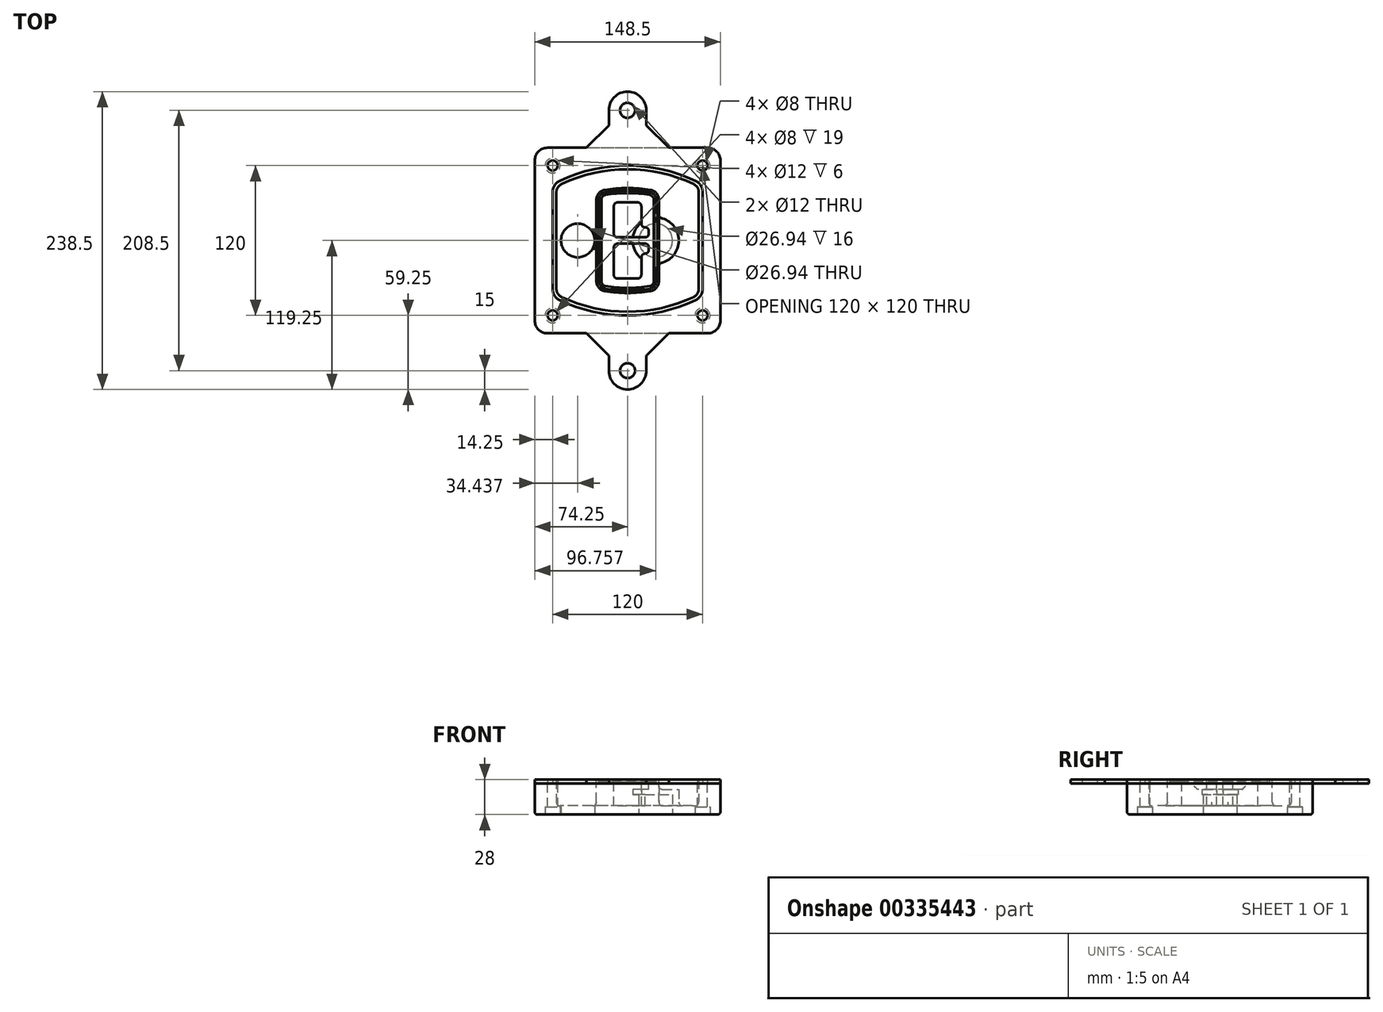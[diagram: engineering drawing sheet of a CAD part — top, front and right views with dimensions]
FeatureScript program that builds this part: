
annotation { "Feature Type Name" : "Feature", "Feature Type Description" : "" }
export const myFeature = defineFeature(function(context is Context, id is Id, definition is map)
    precondition{}
    {
        {
            var Q0;
            Q0=qCreatedBy(makeId("Top.planeOp"),FACE);
            var sketch = newSketch(context, id + "F0", { "sketchPlane" : qUnion([Q0])});
            skPoint(sketch, "E0.rect.middle", {"position": v(0, 0) * mm});
            skLineSegment(sketch, "E1.bottom", {"start": v(-64.25, -74.25) * mm, "end": v(64.25, -74.25) * mm});
            skLineSegment(sketch, "E1.top", {"start": v(-64.25, 74.25) * mm, "end": v(64.25, 74.25) * mm});
            skLineSegment(sketch, "E1.left", {"start": v(-74.25, -64.25) * mm, "end": v(-74.25, 64.25) * mm});
            skLineSegment(sketch, "E1.right", {"start": v(74.25, -64.25) * mm, "end": v(74.25, 64.25) * mm});
            skLineSegment(sketch, "E2", {"start": v(-74.25, 74.25) * mm, "end": v(74.25, -74.25) * mm, "construction": true});
            skLineSegment(sketch, "E3", {"start": v(74.25, 74.25) * mm, "end": v(-74.25, -74.25) * mm, "construction": true});
            skCircle(sketch, "E4", {"center": v(-60, 60) * mm, "radius": 4 * mm});
            skCircle(sketch, "E5", {"center": v(60, 60) * mm, "radius": 4 * mm});
            skCircle(sketch, "E6", {"center": v(60, -60) * mm, "radius": 4 * mm});
            skCircle(sketch, "E7", {"center": v(-60, -60) * mm, "radius": 4 * mm});
            skLineSegment(sketch, "E8", {"start": v(-60, 60) * mm, "end": v(60, 60) * mm, "construction": true});
            skLineSegment(sketch, "E9", {"start": v(60, 60) * mm, "end": v(60, -60) * mm, "construction": true});
            skLineSegment(sketch, "E10", {"start": v(60, -60) * mm, "end": v(-60, -60) * mm, "construction": true});
            skLineSegment(sketch, "E11", {"start": v(-60, -60) * mm, "end": v(-60, 60) * mm, "construction": true});
            skLineSegment(sketch, "E12", {"start": v(-60, 38.83) * mm, "end": v(-60, -38.83) * mm});
            skLineSegment(sketch, "E13", {"start": v(60, 38.83) * mm, "end": v(60, -38.83) * mm});
            skArc(sketch, "E14", {"start": v(54.26, 47.88) * mm, "mid": v(0, 60) * mm, "end": v(-54.26, 47.88) * mm});
            skArc(sketch, "E15", {"start": v(-54.26, -47.88) * mm, "mid": v(0, -60) * mm, "end": v(54.26, -47.88) * mm});
            skLineSegment(sketch, "E16", {"start": v(-60, 0) * mm, "end": v(60, 0) * mm, "construction": true});
            skPoint(sketch, "E17.visualSharp", {"position": v(-60, -45) * mm});
            skArc(sketch, "E17.filletArc", {"start": v(-60, -38.83) * mm, "mid": v(-58.44, -44.2) * mm, "end": v(-54.26, -47.88) * mm});
            skPoint(sketch, "E18.visualSharp", {"position": v(-60, 45) * mm});
            skArc(sketch, "E18.filletArc", {"start": v(-54.26, 47.88) * mm, "mid": v(-58.44, 44.2) * mm, "end": v(-60, 38.83) * mm});
            skPoint(sketch, "E19.visualSharp", {"position": v(60, 45) * mm});
            skArc(sketch, "E19.filletArc", {"start": v(60, 38.83) * mm, "mid": v(58.44, 44.2) * mm, "end": v(54.26, 47.88) * mm});
            skPoint(sketch, "E20.visualSharp", {"position": v(60, -45) * mm});
            skArc(sketch, "E20.filletArc", {"start": v(54.26, -47.88) * mm, "mid": v(58.44, -44.2) * mm, "end": v(60, -38.83) * mm});
            skPoint(sketch, "E21.visualSharp", {"position": v(-74.25, 74.25) * mm});
            skArc(sketch, "E21.filletArc", {"start": v(-64.25, 74.25) * mm, "mid": v(-71.32, 71.32) * mm, "end": v(-74.25, 64.25) * mm});
            skPoint(sketch, "E22.visualSharp", {"position": v(74.25, 74.25) * mm});
            skArc(sketch, "E22.filletArc", {"start": v(74.25, 64.25) * mm, "mid": v(71.32, 71.32) * mm, "end": v(64.25, 74.25) * mm});
            skPoint(sketch, "E23.visualSharp", {"position": v(74.25, -74.25) * mm});
            skArc(sketch, "E23.filletArc", {"start": v(64.25, -74.25) * mm, "mid": v(71.32, -71.32) * mm, "end": v(74.25, -64.25) * mm});
            skPoint(sketch, "E24.visualSharp", {"position": v(-74.25, -74.25) * mm});
            skArc(sketch, "E24.filletArc", {"start": v(-74.25, -64.25) * mm, "mid": v(-71.32, -71.32) * mm, "end": v(-64.25, -74.25) * mm});
            skArc(sketch, "E25.0", {"start": v(57, 38.83) * mm, "mid": v(55.9, 42.58) * mm, "end": v(52.98, 45.17) * mm});
            skLineSegment(sketch, "E25.1", {"start": v(57, 38.83) * mm, "end": v(57, -38.83) * mm});
            skArc(sketch, "E25.2", {"start": v(52.98, -45.17) * mm, "mid": v(55.9, -42.58) * mm, "end": v(57, -38.83) * mm});
            skArc(sketch, "E25.3", {"start": v(-52.98, -45.17) * mm, "mid": v(0, -57) * mm, "end": v(52.98, -45.17) * mm});
            skArc(sketch, "E25.4", {"start": v(-57, -38.83) * mm, "mid": v(-55.9, -42.58) * mm, "end": v(-52.98, -45.17) * mm});
            skArc(sketch, "E25.5", {"start": v(52.98, 45.17) * mm, "mid": v(0, 57) * mm, "end": v(-52.98, 45.17) * mm});
            skLineSegment(sketch, "E25.6", {"start": v(-57, 38.83) * mm, "end": v(-57, -38.83) * mm});
            skArc(sketch, "E25.7", {"start": v(-52.98, 45.17) * mm, "mid": v(-55.9, 42.58) * mm, "end": v(-57, 38.83) * mm});
            skArc(sketch, "E26.0", {"start": v(-55.96, 51.5) * mm, "mid": v(-61.82, 46.33) * mm, "end": v(-64, 38.83) * mm});
            skArc(sketch, "E26.1", {"start": v(55.96, 51.5) * mm, "mid": v(0, 64) * mm, "end": v(-55.96, 51.5) * mm});
            skArc(sketch, "E26.2", {"start": v(64, 38.83) * mm, "mid": v(61.82, 46.33) * mm, "end": v(55.96, 51.5) * mm});
            skLineSegment(sketch, "E26.3", {"start": v(64, 38.83) * mm, "end": v(64, -38.83) * mm});
            skArc(sketch, "E26.4", {"start": v(55.96, -51.5) * mm, "mid": v(61.82, -46.33) * mm, "end": v(64, -38.83) * mm});
            skLineSegment(sketch, "E26.5", {"start": v(-64, 38.83) * mm, "end": v(-64, -38.83) * mm});
            skArc(sketch, "E26.6", {"start": v(-55.96, -51.5) * mm, "mid": v(0, -64) * mm, "end": v(55.96, -51.5) * mm});
            skArc(sketch, "E26.7", {"start": v(-64, -38.83) * mm, "mid": v(-61.82, -46.33) * mm, "end": v(-55.96, -51.5) * mm});
            skSolve(sketch);
        }
        {
            var Q0;
            Q0=makeQuery(id+"F0.imprint","IMPRINT",FACE,{"disambiguationData":[TD([[makeQuery(id+"F0.imprint","IMPRINT",EDGE,{"derivedFrom":sQuery(id+"F0.wireOp",EDGE,"E1.bottom")}),1.0]])]});
            var Q1;
            Q1=makeQuery(id+"F0.imprint","IMPRINT",FACE,{"disambiguationData":[TD([[makeQuery(id+"F0.imprint","IMPRINT",EDGE,{"derivedFrom":sQuery(id+"F0.wireOp",EDGE,"E12")}),1.0]])]});
            var Q2;
            Q2=makeQuery(id+"F0.imprint","IMPRINT",FACE,{"disambiguationData":[TD([[makeQuery(id+"F0.imprint","IMPRINT",EDGE,{"derivedFrom":sQuery(id+"F0.wireOp",EDGE,"E25.0")}),1.0]])]});
            var Q3;
            Q3=makeQuery(id+"F0.imprint","IMPRINT",FACE,{"disambiguationData":[TD([[makeQuery(id+"F0.imprint","IMPRINT",EDGE,{"derivedFrom":sQuery(id+"F0.wireOp",EDGE,"E12")}),-1.0]])]});
            extrude(context, id + "F1", {"entities" : qUnion([Q0, Q1, Q2, Q3]), "oppositeDirection" : true, "depth" : 25 * mm});
        }
        {
            var Q0;
            Q0=makeQuery(id+"F0.imprint","IMPRINT",FACE,{"disambiguationData":[TD([[makeQuery(id+"F0.imprint","IMPRINT",EDGE,{"derivedFrom":sQuery(id+"F0.wireOp",EDGE,"E12")}),1.0]])]});
            extrude(context, id + "F2", {"entities" : qUnion([Q0]), "operationType" : NewBodyOperationType.ADD, "depth" : 3 * mm});
        }
        {
            var Q0;
            Q0=makeQuery(id+"F0.imprint","IMPRINT",FACE,{"disambiguationData":[TD([[makeQuery(id+"F0.imprint","IMPRINT",EDGE,{"derivedFrom":sQuery(id+"F0.wireOp",EDGE,"E25.0")}),1.0]])]});
            extrude(context, id + "F3", {"entities" : qUnion([Q0]), "operationType" : NewBodyOperationType.REMOVE, "oppositeDirection" : true, "depth" : 18 * mm});
        }
        {
            var Q0;
            Q0=makeQuery(id+"F2.opExtrude","CAP_FACE",FACE,{"disambiguationData":[OSD([sQuery(id+"F0.wireOp",EDGE,"E12"),sQuery(id+"F0.wireOp",EDGE,"E13"),sQuery(id+"F0.wireOp",EDGE,"E14"),sQuery(id+"F0.wireOp",EDGE,"E15"),sQuery(id+"F0.wireOp",EDGE,"E17.filletArc"),sQuery(id+"F0.wireOp",EDGE,"E18.filletArc"),sQuery(id+"F0.wireOp",EDGE,"E19.filletArc"),sQuery(id+"F0.wireOp",EDGE,"E20.filletArc"),sQuery(id+"F0.wireOp",EDGE,"E25.0"),sQuery(id+"F0.wireOp",EDGE,"E25.1"),sQuery(id+"F0.wireOp",EDGE,"E25.2"),sQuery(id+"F0.wireOp",EDGE,"E25.3"),sQuery(id+"F0.wireOp",EDGE,"E25.4"),sQuery(id+"F0.wireOp",EDGE,"E25.5"),sQuery(id+"F0.wireOp",EDGE,"E25.6"),sQuery(id+"F0.wireOp",EDGE,"E25.7")])],"isStart":false});
            var sketch = newSketch(context, id + "F4", { "sketchPlane" : qUnion([Q0])});
            skArc(sketch, "E27.0", {"start": v(-18.34, -40.45) * mm, "mid": v(0, -42) * mm, "end": v(18.34, -40.45) * mm});
            skArc(sketch, "E28.0", {"start": v(18.34, 40.45) * mm, "mid": v(0, 42) * mm, "end": v(-18.34, 40.45) * mm});
            skLineSegment(sketch, "E29", {"start": v(-25, 32.57) * mm, "end": v(-25, -32.57) * mm});
            skLineSegment(sketch, "E30", {"start": v(25, 32.57) * mm, "end": v(25, -32.57) * mm});
            skLineSegment(sketch, "E31", {"start": v(-25, 39.1) * mm, "end": v(25, 39.1) * mm, "construction": true});
            skLineSegment(sketch, "E32", {"start": v(-25, -39.1) * mm, "end": v(25, -39.1) * mm, "construction": true});
            skPoint(sketch, "E33.visualSharp", {"position": v(-25, 39.1) * mm});
            skArc(sketch, "E33.filletArc", {"start": v(-18.34, 40.45) * mm, "mid": v(-23.11, 37.73) * mm, "end": v(-25, 32.57) * mm});
            skPoint(sketch, "E34.visualSharp", {"position": v(25, 39.1) * mm});
            skArc(sketch, "E34.filletArc", {"start": v(25, 32.57) * mm, "mid": v(23.11, 37.73) * mm, "end": v(18.34, 40.45) * mm});
            skPoint(sketch, "E35.visualSharp", {"position": v(25, -39.1) * mm});
            skArc(sketch, "E35.filletArc", {"start": v(18.34, -40.45) * mm, "mid": v(23.11, -37.73) * mm, "end": v(25, -32.57) * mm});
            skPoint(sketch, "E36.visualSharp", {"position": v(-25, -39.1) * mm});
            skArc(sketch, "E36.filletArc", {"start": v(-25, -32.57) * mm, "mid": v(-23.11, -37.73) * mm, "end": v(-18.34, -40.45) * mm});
            skArc(sketch, "E37.0", {"start": v(52.98, 45.17) * mm, "mid": v(0, 57) * mm, "end": v(-52.98, 45.17) * mm});
            skArc(sketch, "E37.1", {"start": v(-52.98, 45.17) * mm, "mid": v(-55.9, 42.58) * mm, "end": v(-57, 38.83) * mm});
            skLineSegment(sketch, "E37.2", {"start": v(-57, 38.83) * mm, "end": v(-57, -38.83) * mm});
            skArc(sketch, "E37.3", {"start": v(-57, -38.83) * mm, "mid": v(-55.9, -42.58) * mm, "end": v(-52.98, -45.17) * mm});
            skArc(sketch, "E37.4", {"start": v(-52.98, -45.17) * mm, "mid": v(0, -57) * mm, "end": v(52.98, -45.17) * mm});
            skArc(sketch, "E37.5", {"start": v(52.98, -45.17) * mm, "mid": v(55.9, -42.58) * mm, "end": v(57, -38.83) * mm});
            skLineSegment(sketch, "E37.6", {"start": v(57, 38.83) * mm, "end": v(57, -38.83) * mm});
            skArc(sketch, "E37.7", {"start": v(57, 38.83) * mm, "mid": v(55.9, 42.58) * mm, "end": v(52.98, 45.17) * mm});
            skLineSegment(sketch, "E38.0", {"start": v(23, 32.57) * mm, "end": v(23, -32.57) * mm});
            skArc(sketch, "E38.1", {"start": v(18, -38.48) * mm, "mid": v(21.58, -36.44) * mm, "end": v(23, -32.57) * mm});
            skArc(sketch, "E38.2", {"start": v(-18, -38.48) * mm, "mid": v(0, -40) * mm, "end": v(18, -38.48) * mm});
            skArc(sketch, "E38.3", {"start": v(-23, -32.57) * mm, "mid": v(-21.58, -36.44) * mm, "end": v(-18, -38.48) * mm});
            skLineSegment(sketch, "E38.4", {"start": v(-23, 32.57) * mm, "end": v(-23, -32.57) * mm});
            skArc(sketch, "E38.5", {"start": v(23, 32.57) * mm, "mid": v(21.58, 36.44) * mm, "end": v(18, 38.48) * mm});
            skArc(sketch, "E38.6", {"start": v(-18, 38.48) * mm, "mid": v(-21.58, 36.44) * mm, "end": v(-23, 32.57) * mm});
            skArc(sketch, "E38.7", {"start": v(18, 38.48) * mm, "mid": v(0, 40) * mm, "end": v(-18, 38.48) * mm});
            skArc(sketch, "E39.0", {"start": v(21, 32.57) * mm, "mid": v(20.06, 35.15) * mm, "end": v(17.67, 36.5) * mm});
            skLineSegment(sketch, "E39.1", {"start": v(21, 32.57) * mm, "end": v(21, -32.57) * mm});
            skArc(sketch, "E39.2", {"start": v(17.67, -36.5) * mm, "mid": v(20.06, -35.15) * mm, "end": v(21, -32.57) * mm});
            skArc(sketch, "E39.3", {"start": v(-17.67, -36.5) * mm, "mid": v(0, -38) * mm, "end": v(17.67, -36.5) * mm});
            skArc(sketch, "E39.4", {"start": v(-21, -32.57) * mm, "mid": v(-20.06, -35.15) * mm, "end": v(-17.67, -36.5) * mm});
            skArc(sketch, "E39.5", {"start": v(17.67, 36.5) * mm, "mid": v(0, 38) * mm, "end": v(-17.67, 36.5) * mm});
            skLineSegment(sketch, "E39.6", {"start": v(-21, 32.57) * mm, "end": v(-21, -32.57) * mm});
            skArc(sketch, "E39.7", {"start": v(-17.67, 36.5) * mm, "mid": v(-20.06, 35.15) * mm, "end": v(-21, 32.57) * mm});
            skLineSegment(sketch, "E40", {"start": v(-25, 0) * mm, "end": v(25, 0) * mm, "construction": true});
            skLineSegment(sketch, "E41", {"start": v(-11, 5.5) * mm, "end": v(-11, 27.5) * mm});
            skLineSegment(sketch, "E42", {"start": v(-8, 30.5) * mm, "end": v(8, 30.5) * mm});
            skLineSegment(sketch, "E43", {"start": v(11, 27.5) * mm, "end": v(11, 13.5) * mm});
            skLineSegment(sketch, "E44", {"start": v(14, 10.5) * mm, "end": v(14, 10.5) * mm});
            skLineSegment(sketch, "E45", {"start": v(17, 7.5) * mm, "end": v(17, 5.5) * mm});
            skLineSegment(sketch, "E46", {"start": v(14, 2.5) * mm, "end": v(-8, 2.5) * mm});
            skPoint(sketch, "E47.visualSharp", {"position": v(-11, 30.5) * mm});
            skArc(sketch, "E47.filletArc", {"start": v(-8, 30.5) * mm, "mid": v(-10.12, 29.62) * mm, "end": v(-11, 27.5) * mm});
            skPoint(sketch, "E48.visualSharp", {"position": v(11, 30.5) * mm});
            skArc(sketch, "E48.filletArc", {"start": v(11, 27.5) * mm, "mid": v(10.12, 29.62) * mm, "end": v(8, 30.5) * mm});
            skPoint(sketch, "E49.visualSharp", {"position": v(11, 10.5) * mm});
            skArc(sketch, "E49.filletArc", {"start": v(11, 13.5) * mm, "mid": v(11.88, 11.38) * mm, "end": v(14, 10.5) * mm});
            skPoint(sketch, "E50.visualSharp", {"position": v(17, 10.5) * mm});
            skArc(sketch, "E50.filletArc", {"start": v(17, 7.5) * mm, "mid": v(16.12, 9.62) * mm, "end": v(14, 10.5) * mm});
            skPoint(sketch, "E51.visualSharp", {"position": v(17, 2.5) * mm});
            skArc(sketch, "E51.filletArc", {"start": v(14, 2.5) * mm, "mid": v(16.12, 3.38) * mm, "end": v(17, 5.5) * mm});
            skPoint(sketch, "E52.visualSharp", {"position": v(-11, 2.5) * mm});
            skArc(sketch, "E52.filletArc", {"start": v(-11, 5.5) * mm, "mid": v(-10.12, 3.38) * mm, "end": v(-8, 2.5) * mm});
            skLineSegment(sketch, "E53.0.MirrorCS", {"start": v(14, -2.5) * mm, "end": v(-8, -2.5) * mm});
            skArc(sketch, "E54.0.MirrorCS", {"start": v(-11, -5.5) * mm, "mid": v(-10.12, -3.38) * mm, "end": v(-8, -2.5) * mm});
            skLineSegment(sketch, "E55.0.MirrorCS", {"start": v(-11, -5.5) * mm, "end": v(-11, -27.5) * mm});
            skArc(sketch, "E56.0.MirrorCS", {"start": v(-8, -30.5) * mm, "mid": v(-10.12, -29.62) * mm, "end": v(-11, -27.5) * mm});
            skLineSegment(sketch, "E57.0.MirrorCS", {"start": v(-8, -30.5) * mm, "end": v(8, -30.5) * mm});
            skArc(sketch, "E58.0.MirrorCS", {"start": v(11, -27.5) * mm, "mid": v(10.12, -29.62) * mm, "end": v(8, -30.5) * mm});
            skLineSegment(sketch, "E59.0.MirrorCS", {"start": v(11, -27.5) * mm, "end": v(11, -13.5) * mm});
            skArc(sketch, "E60.0.MirrorCS", {"start": v(11, -13.5) * mm, "mid": v(11.88, -11.38) * mm, "end": v(14, -10.5) * mm});
            skArc(sketch, "E61.0.MirrorCS", {"start": v(17, -7.5) * mm, "mid": v(16.12, -9.62) * mm, "end": v(14, -10.5) * mm});
            skLineSegment(sketch, "E62.0.MirrorCS", {"start": v(17, -7.5) * mm, "end": v(17, -5.5) * mm});
            skArc(sketch, "E63.0.MirrorCS", {"start": v(14, -2.5) * mm, "mid": v(16.12, -3.38) * mm, "end": v(17, -5.5) * mm});
            skSolve(sketch);
        }
        {
            var Q0;
            Q0=makeQuery(id+"F4.imprint","IMPRINT",FACE,{"disambiguationData":[TD([[makeQuery(id+"F4.imprint","IMPRINT",EDGE,{"derivedFrom":sQuery(id+"F4.wireOp",EDGE,"E27.0")}),1.0]])]});
            var Q1;
            Q1=makeQuery(id+"F4.imprint","IMPRINT",FACE,{"disambiguationData":[TD([[makeQuery(id+"F4.imprint","IMPRINT",EDGE,{"derivedFrom":sQuery(id+"F4.wireOp",EDGE,"E38.0")}),-1.0]])]});
            var Q2;
            Q2=makeQuery(id+"F4.imprint","IMPRINT",FACE,{"disambiguationData":[TD([[makeQuery(id+"F4.imprint","IMPRINT",EDGE,{"derivedFrom":sQuery(id+"F4.wireOp",EDGE,"E39.0")}),1.0]])]});
            extrude(context, id + "F5", {"entities" : qUnion([Q0, Q1, Q2]), "operationType" : NewBodyOperationType.ADD, "endBound" : BoundingType.UP_TO_NEXT, "oppositeDirection" : true, "depth" : 25 * mm});
        }
        {
            var Q0;
            Q0=makeQuery(id+"F4.imprint","IMPRINT",FACE,{"disambiguationData":[TD([[makeQuery(id+"F4.imprint","IMPRINT",EDGE,{"derivedFrom":sQuery(id+"F4.wireOp",EDGE,"E38.0")}),-1.0]])]});
            extrude(context, id + "F6", {"entities" : qUnion([Q0]), "operationType" : NewBodyOperationType.REMOVE, "oppositeDirection" : true, "depth" : 2 * mm});
        }
        {
            var Q0;
            Q0=makeQuery(id+"F1.opExtrude","CAP_FACE",FACE,{"disambiguationData":[OSD([sQuery(id+"F0.wireOp",EDGE,"E1.bottom"),sQuery(id+"F0.wireOp",EDGE,"E1.top"),sQuery(id+"F0.wireOp",EDGE,"E1.left"),sQuery(id+"F0.wireOp",EDGE,"E1.right"),sQuery(id+"F0.wireOp",EDGE,"E4"),sQuery(id+"F0.wireOp",EDGE,"E5"),sQuery(id+"F0.wireOp",EDGE,"E6"),sQuery(id+"F0.wireOp",EDGE,"E7"),sQuery(id+"F0.wireOp",EDGE,"E21.filletArc"),sQuery(id+"F0.wireOp",EDGE,"E22.filletArc"),sQuery(id+"F0.wireOp",EDGE,"E23.filletArc"),sQuery(id+"F0.wireOp",EDGE,"E24.filletArc")])],"isStart":false});
            var sketch = newSketch(context, id + "F7", { "sketchPlane" : qUnion([Q0])});
            skCircle(sketch, "E64", {"center": v(22.5, 0) * mm, "radius": 13.47 * mm});
            skCircle(sketch, "E65", {"center": v(-39.81, 0) * mm, "radius": 13.47 * mm});
            skLineSegment(sketch, "E66", {"start": v(74.25, 0) * mm, "end": v(-74.25, 0) * mm});
            skCircle(sketch, "E67", {"center": v(22.5, 0) * mm, "radius": 18.47 * mm});
            skCircle(sketch, "E68", {"center": v(60, -60) * mm, "radius": 6 * mm});
            skCircle(sketch, "E69", {"center": v(-60, -60) * mm, "radius": 6 * mm});
            skCircle(sketch, "E70", {"center": v(-60, 60) * mm, "radius": 6 * mm});
            skCircle(sketch, "E71", {"center": v(60, 60) * mm, "radius": 6 * mm});
            skSolve(sketch);
        }
        {
            var Q0;
            {var subQ1=sQuery(id+"F7.wireOp",EDGE,"E66");var subQ4=sQuery(id+"F7.wireOp",EDGE,"E64");var subQ6=makeQuery(id+"F7.imprint","INTERSECT",VERTEX,{"disambiguationData":[OD(0.0)],"derivedFrom":[subQ4,subQ1]});Q0=makeQuery(id+"F7.imprint","IMPRINT",FACE,{"disambiguationData":[TD([[makeQuery(id+"F7.imprint","IMPRINT",EDGE,{"disambiguationData":[TD([[subQ6,-1.0]])],"derivedFrom":subQ4}),-1.0]])]});}
            var Q1;
            {var subQ0=sQuery(id+"F7.wireOp",EDGE,"E66");var subQ1=sQuery(id+"F7.wireOp",EDGE,"E64");var subQ3=makeQuery(id+"F7.imprint","INTERSECT",VERTEX,{"disambiguationData":[OD(0.0)],"derivedFrom":[subQ1,subQ0]});Q1=makeQuery(id+"F7.imprint","IMPRINT",FACE,{"disambiguationData":[TD([[makeQuery(id+"F7.imprint","IMPRINT",EDGE,{"disambiguationData":[TD([[subQ3,-1.0]])],"derivedFrom":subQ1}),1.0]])]});}
            var Q2;
            {var subQ0=sQuery(id+"F7.wireOp",EDGE,"E66");var subQ1=sQuery(id+"F7.wireOp",EDGE,"E64");var subQ3=makeQuery(id+"F7.imprint","INTERSECT",VERTEX,{"disambiguationData":[OD(0.0)],"derivedFrom":[subQ1,subQ0]});Q2=makeQuery(id+"F7.imprint","IMPRINT",FACE,{"disambiguationData":[TD([[makeQuery(id+"F7.imprint","IMPRINT",EDGE,{"disambiguationData":[TD([[subQ3,1.0]])],"derivedFrom":subQ1}),1.0]])]});}
            var Q3;
            {var subQ1=sQuery(id+"F7.wireOp",EDGE,"E66");var subQ4=sQuery(id+"F7.wireOp",EDGE,"E64");var subQ6=makeQuery(id+"F7.imprint","INTERSECT",VERTEX,{"disambiguationData":[OD(0.0)],"derivedFrom":[subQ4,subQ1]});Q3=makeQuery(id+"F7.imprint","IMPRINT",FACE,{"disambiguationData":[TD([[makeQuery(id+"F7.imprint","IMPRINT",EDGE,{"disambiguationData":[TD([[subQ6,1.0]])],"derivedFrom":subQ4}),-1.0]])]});}
            extrude(context, id + "F8", {"entities" : qUnion([Q0, Q1, Q2, Q3]), "operationType" : NewBodyOperationType.ADD, "oppositeDirection" : true, "depth" : 20 * mm});
        }
        {
            var Q0;
            {var subQ0=sQuery(id+"F7.wireOp",EDGE,"E66");var subQ1=sQuery(id+"F7.wireOp",EDGE,"E64");var subQ3=makeQuery(id+"F7.imprint","INTERSECT",VERTEX,{"disambiguationData":[OD(0.0)],"derivedFrom":[subQ1,subQ0]});Q0=makeQuery(id+"F7.imprint","IMPRINT",FACE,{"disambiguationData":[TD([[makeQuery(id+"F7.imprint","IMPRINT",EDGE,{"disambiguationData":[TD([[subQ3,-1.0]])],"derivedFrom":subQ1}),1.0]])]});}
            var Q1;
            {var subQ0=sQuery(id+"F7.wireOp",EDGE,"E66");var subQ1=sQuery(id+"F7.wireOp",EDGE,"E64");var subQ3=makeQuery(id+"F7.imprint","INTERSECT",VERTEX,{"disambiguationData":[OD(0.0)],"derivedFrom":[subQ1,subQ0]});Q1=makeQuery(id+"F7.imprint","IMPRINT",FACE,{"disambiguationData":[TD([[makeQuery(id+"F7.imprint","IMPRINT",EDGE,{"disambiguationData":[TD([[subQ3,1.0]])],"derivedFrom":subQ1}),1.0]])]});}
            extrude(context, id + "F9", {"entities" : qUnion([Q0, Q1]), "operationType" : NewBodyOperationType.REMOVE, "oppositeDirection" : true, "depth" : 16 * mm});
        }
        {
            var Q0;
            {var subQ0=sQuery(id+"F7.wireOp",EDGE,"E66");var subQ1=sQuery(id+"F7.wireOp",EDGE,"E65");var subQ3=makeQuery(id+"F7.imprint","INTERSECT",VERTEX,{"disambiguationData":[OD(0.0)],"derivedFrom":[subQ1,subQ0]});Q0=makeQuery(id+"F7.imprint","IMPRINT",FACE,{"disambiguationData":[TD([[makeQuery(id+"F7.imprint","IMPRINT",EDGE,{"disambiguationData":[TD([[subQ3,-1.0]])],"derivedFrom":subQ1}),1.0]])]});}
            var Q1;
            {var subQ0=sQuery(id+"F7.wireOp",EDGE,"E66");var subQ1=sQuery(id+"F7.wireOp",EDGE,"E65");var subQ3=makeQuery(id+"F7.imprint","INTERSECT",VERTEX,{"disambiguationData":[OD(0.0)],"derivedFrom":[subQ1,subQ0]});Q1=makeQuery(id+"F7.imprint","IMPRINT",FACE,{"disambiguationData":[TD([[makeQuery(id+"F7.imprint","IMPRINT",EDGE,{"disambiguationData":[TD([[subQ3,1.0]])],"derivedFrom":subQ1}),1.0]])]});}
            extrude(context, id + "F10", {"entities" : qUnion([Q0, Q1]), "operationType" : NewBodyOperationType.REMOVE, "oppositeDirection" : true, "depth" : 25 * mm});
        }
        {
            var Q0;
            Q0=makeQuery(id+"F7.imprint","IMPRINT",FACE,{"disambiguationData":[TD([[makeQuery(id+"F7.imprint","IMPRINT",EDGE,{"derivedFrom":sQuery(id+"F7.wireOp",EDGE,"E68")}),1.0]])]});
            var Q1;
            Q1=makeQuery(id+"F7.imprint","IMPRINT",FACE,{"disambiguationData":[TD([[makeQuery(id+"F7.imprint","IMPRINT",EDGE,{"derivedFrom":makeQuery(id+"F1.opExtrude","CAP_EDGE",EDGE,{"disambiguationData":[OSD([sQuery(id+"F0.wireOp",EDGE,"E5")])],"isStart":false})}),-1.0]])]});
            var Q2;
            Q2=makeQuery(id+"F7.imprint","IMPRINT",FACE,{"disambiguationData":[TD([[makeQuery(id+"F7.imprint","IMPRINT",EDGE,{"derivedFrom":sQuery(id+"F7.wireOp",EDGE,"E69")}),1.0]])]});
            var Q3;
            Q3=makeQuery(id+"F7.imprint","IMPRINT",FACE,{"disambiguationData":[TD([[makeQuery(id+"F7.imprint","IMPRINT",EDGE,{"derivedFrom":makeQuery(id+"F1.opExtrude","CAP_EDGE",EDGE,{"disambiguationData":[OSD([sQuery(id+"F0.wireOp",EDGE,"E4")])],"isStart":false})}),-1.0]])]});
            var Q4;
            Q4=makeQuery(id+"F7.imprint","IMPRINT",FACE,{"disambiguationData":[TD([[makeQuery(id+"F7.imprint","IMPRINT",EDGE,{"derivedFrom":sQuery(id+"F7.wireOp",EDGE,"E70")}),1.0]])]});
            var Q5;
            Q5=makeQuery(id+"F7.imprint","IMPRINT",FACE,{"disambiguationData":[TD([[makeQuery(id+"F7.imprint","IMPRINT",EDGE,{"derivedFrom":makeQuery(id+"F1.opExtrude","CAP_EDGE",EDGE,{"disambiguationData":[OSD([sQuery(id+"F0.wireOp",EDGE,"E7")])],"isStart":false})}),-1.0]])]});
            var Q6;
            Q6=makeQuery(id+"F7.imprint","IMPRINT",FACE,{"disambiguationData":[TD([[makeQuery(id+"F7.imprint","IMPRINT",EDGE,{"derivedFrom":sQuery(id+"F7.wireOp",EDGE,"E71")}),1.0]])]});
            var Q7;
            Q7=makeQuery(id+"F7.imprint","IMPRINT",FACE,{"disambiguationData":[TD([[makeQuery(id+"F7.imprint","IMPRINT",EDGE,{"derivedFrom":makeQuery(id+"F1.opExtrude","CAP_EDGE",EDGE,{"disambiguationData":[OSD([sQuery(id+"F0.wireOp",EDGE,"E6")])],"isStart":false})}),-1.0]])]});
            extrude(context, id + "F11", {"entities" : qUnion([Q0, Q1, Q2, Q3, Q4, Q5, Q6, Q7]), "operationType" : NewBodyOperationType.REMOVE, "oppositeDirection" : true, "depth" : 6 * mm});
        }
        {
            var Q0;
            Q0=makeQuery(id+"F9.boolean.opBoolean","COPY",FACE,{"derivedFrom":makeQuery(id+"F9.opExtrude","CAP_FACE",FACE,{"disambiguationData":[OSD([sQuery(id+"F7.wireOp",EDGE,"E64")])],"isStart":false})});
            var sketch = newSketch(context, id + "F12", { "sketchPlane" : qUnion([Q0])});
            skArc(sketch, "E72.0", {"start": v(11, 14.45) * mm, "mid": v(6.45, 9.13) * mm, "end": v(4.2, 2.5) * mm});
            skArc(sketch, "E72.1", {"start": v(4.2, -2.5) * mm, "mid": v(6.45, -9.13) * mm, "end": v(11, -14.45) * mm});
            skLineSegment(sketch, "E73", {"start": v(4.2, -2.5) * mm, "end": v(14, -2.5) * mm});
            skLineSegment(sketch, "E74.0", {"start": v(14, 2.5) * mm, "end": v(4.2, 2.5) * mm});
            skArc(sketch, "E74.1", {"start": v(14, 2.5) * mm, "mid": v(16.12, 3.38) * mm, "end": v(17, 5.5) * mm});
            skLineSegment(sketch, "E74.2", {"start": v(17, 7.5) * mm, "end": v(17, 5.5) * mm});
            skArc(sketch, "E74.3", {"start": v(17, 7.5) * mm, "mid": v(16.12, 9.62) * mm, "end": v(14, 10.5) * mm});
            skArc(sketch, "E74.4", {"start": v(11, 13.5) * mm, "mid": v(11.88, 11.38) * mm, "end": v(14, 10.5) * mm});
            skLineSegment(sketch, "E74.5", {"start": v(11, 14.45) * mm, "end": v(11, 13.5) * mm});
            skLineSegment(sketch, "E74.7", {"start": v(14, -2.5) * mm, "end": v(4.2, -2.5) * mm});
            skArc(sketch, "E74.8", {"start": v(14, -2.5) * mm, "mid": v(16.12, -3.38) * mm, "end": v(17, -5.5) * mm});
            skLineSegment(sketch, "E74.9", {"start": v(17, -7.5) * mm, "end": v(17, -5.5) * mm});
            skArc(sketch, "E74.10", {"start": v(17, -7.5) * mm, "mid": v(16.12, -9.62) * mm, "end": v(14, -10.5) * mm});
            skArc(sketch, "E74.11", {"start": v(11, -13.5) * mm, "mid": v(11.88, -11.38) * mm, "end": v(14, -10.5) * mm});
            skLineSegment(sketch, "E74.12", {"start": v(11, -14.45) * mm, "end": v(11, -13.5) * mm});
            skPoint(sketch, "E75.orphan", {"position": v(11, -27.5) * mm});
            skPoint(sketch, "E76.orphan", {"position": v(-8, -2.5) * mm});
            skPoint(sketch, "E77.orphan", {"position": v(-8, 2.5) * mm});
            skPoint(sketch, "E78.orphan", {"position": v(11, 27.5) * mm});
            skSolve(sketch);
        }
        {
            var Q0;
            {var subQ7=sQuery(id+"F12.wireOp",EDGE,"E72.0");var subQ14=sQuery(id+"F12.wireOp",EDGE,"E72.1");var subQ16=sQuery(id+"F12.wireOp",EDGE,"E74.1");var subQ18=sQuery(id+"F12.wireOp",EDGE,"E74.8");Q0=qUnion([makeQuery(id+"F12.imprint","IMPRINT",FACE,{"disambiguationData":[TD([[makeQuery(id+"F12.imprint","IMPRINT",EDGE,{"derivedFrom":subQ7}),1.0]])]}),makeQuery(id+"F12.imprint","IMPRINT",FACE,{"disambiguationData":[TD([[makeQuery(id+"F12.imprint","IMPRINT",EDGE,{"derivedFrom":subQ14}),1.0]])]}),makeQuery(id+"F12.imprint","IMPRINT",FACE,{"disambiguationData":[TD([[makeQuery(id+"F12.imprint","IMPRINT",EDGE,{"derivedFrom":subQ16}),1.0]])]}),makeQuery(id+"F12.imprint","IMPRINT",FACE,{"disambiguationData":[TD([[makeQuery(id+"F12.imprint","IMPRINT",EDGE,{"derivedFrom":subQ18}),-1.0]])]})]);}
            var Q1;
            Q1=makeQuery(id+"F5.boolean.opBoolean","SPLIT",FACE,{"disambiguationData":[TD([makeQuery(id+"F5.opExtrude","SWEPT_FACE",FACE,{"disambiguationData":[OSD([sQuery(id+"F4.wireOp",EDGE,"E41")])]})])],"derivedFrom":makeQuery(id+"F3.boolean.opBoolean","COPY",FACE,{"derivedFrom":makeQuery(id+"F3.opExtrude","CAP_FACE",FACE,{"disambiguationData":[OSD([sQuery(id+"F0.wireOp",EDGE,"E25.0"),sQuery(id+"F0.wireOp",EDGE,"E25.1"),sQuery(id+"F0.wireOp",EDGE,"E25.2"),sQuery(id+"F0.wireOp",EDGE,"E25.3"),sQuery(id+"F0.wireOp",EDGE,"E25.4"),sQuery(id+"F0.wireOp",EDGE,"E25.5"),sQuery(id+"F0.wireOp",EDGE,"E25.6"),sQuery(id+"F0.wireOp",EDGE,"E25.7")])],"isStart":false})})});
            extrude(context, id + "F13", {"entities" : qUnion([Q0]), "operationType" : NewBodyOperationType.REMOVE, "endBound" : BoundingType.UP_TO_SURFACE, "endBoundEntityFace" : qUnion([Q1]), "depth" : 25 * mm});
        }
        {
            var Q0;
            Q0=makeQuery(id+"F3.boolean.opBoolean","COPY",EDGE,{"derivedFrom":makeQuery(id+"F3.opExtrude","CAP_EDGE",EDGE,{"disambiguationData":[OSD([sQuery(id+"F0.wireOp",EDGE,"E25.6")])],"isStart":false})});
            var Q1;
            Q1=makeQuery(id+"F8.boolean.opBoolean","INTERSECT",EDGE,{"derivedFrom":[makeQuery(id+"F5.opExtrude","SWEPT_FACE",FACE,{"disambiguationData":[OSD([sQuery(id+"F4.wireOp",EDGE,"E30")])]}),makeQuery(id+"F8.opExtrude","CAP_FACE",FACE,{"disambiguationData":[OSD([sQuery(id+"F7.wireOp",EDGE,"E67")])],"isStart":false})]});
            var Q2;
            Q2=makeQuery(id+"F8.boolean.opBoolean","INTERSECT",EDGE,{"disambiguationData":[OD(1.0)],"derivedFrom":[makeQuery(id+"F5.opExtrude","SWEPT_FACE",FACE,{"disambiguationData":[OSD([sQuery(id+"F4.wireOp",EDGE,"E30")])]}),makeQuery(id+"F8.opExtrude","SWEPT_FACE",FACE,{"disambiguationData":[OSD([sQuery(id+"F7.wireOp",EDGE,"E67")])]})]});
            var Q3;
            {var subQ0=sQuery(id+"F4.wireOp",EDGE,"E30");Q3=makeQuery(id+"F8.boolean.opBoolean","SPLIT",EDGE,{"disambiguationData":[TD([makeQuery(id+"F5.opExtrude","SWEPT_FACE",FACE,{"disambiguationData":[OSD([sQuery(id+"F4.wireOp",EDGE,"E35.filletArc")])]})])],"derivedFrom":makeQuery(id+"F5.opExtrude","CAP_EDGE",EDGE,{"disambiguationData":[OSD([subQ0])],"isStart":false})});}
            var Q4;
            {var subQ0=sQuery(id+"F0.wireOp",EDGE,"E25.7");var subQ1=sQuery(id+"F0.wireOp",EDGE,"E25.1");var subQ2=sQuery(id+"F0.wireOp",EDGE,"E25.6");var subQ3=sQuery(id+"F0.wireOp",EDGE,"E25.5");var subQ4=sQuery(id+"F0.wireOp",EDGE,"E25.4");var subQ5=sQuery(id+"F0.wireOp",EDGE,"E25.0");var subQ6=sQuery(id+"F0.wireOp",EDGE,"E25.2");var subQ7=sQuery(id+"F0.wireOp",EDGE,"E25.3");Q4=makeQuery(id+"F8.boolean.opBoolean","INTERSECT",EDGE,{"derivedFrom":[makeQuery(id+"F5.boolean.opBoolean","SPLIT",FACE,{"disambiguationData":[TD([makeQuery(id+"F2.opExtrude","SWEPT_FACE",FACE,{"disambiguationData":[OSD([subQ5])]})])],"derivedFrom":makeQuery(id+"F3.boolean.opBoolean","COPY",FACE,{"derivedFrom":makeQuery(id+"F3.opExtrude","CAP_FACE",FACE,{"disambiguationData":[OSD([subQ5,subQ1,subQ6,subQ7,subQ4,subQ3,subQ2,subQ0])],"isStart":false})})}),makeQuery(id+"F8.opExtrude","SWEPT_FACE",FACE,{"disambiguationData":[OSD([sQuery(id+"F7.wireOp",EDGE,"E67")])]})]});}
            var Q5;
            Q5=makeQuery(id+"F8.boolean.opBoolean","INTERSECT",EDGE,{"disambiguationData":[OD(0.0)],"derivedFrom":[makeQuery(id+"F5.opExtrude","SWEPT_FACE",FACE,{"disambiguationData":[OSD([sQuery(id+"F4.wireOp",EDGE,"E30")])]}),makeQuery(id+"F8.opExtrude","SWEPT_FACE",FACE,{"disambiguationData":[OSD([sQuery(id+"F7.wireOp",EDGE,"E67")])]})]});
            fillet(context, id + "F14", {"entities" : qUnion([Q0, Q1, Q2, Q3, Q4, Q5]), "radius" : 3 * mm, "tangentPropagation" : true, "allowEdgeOverflow" : false});
        }
        {
            var Q0;
            Q0=makeQuery(id+"F1.opExtrude","CAP_EDGE",EDGE,{"disambiguationData":[OSD([sQuery(id+"F0.wireOp",EDGE,"E1.bottom")])],"isStart":false});
            fillet(context, id + "F15", {"entities" : qUnion([Q0]), "radius" : 2 * mm, "tangentPropagation" : true, "allowEdgeOverflow" : false});
        }
        {
            var Q0;
            {var subQ0=sQuery(id+"F0.wireOp",EDGE,"E21.filletArc");var subQ1=sQuery(id+"F0.wireOp",EDGE,"E7");var subQ2=sQuery(id+"F0.wireOp",EDGE,"E6");var subQ3=sQuery(id+"F0.wireOp",EDGE,"E5");var subQ4=sQuery(id+"F0.wireOp",EDGE,"E4");var subQ5=sQuery(id+"F0.wireOp",EDGE,"E22.filletArc");var subQ6=sQuery(id+"F0.wireOp",EDGE,"E1.bottom");var subQ7=sQuery(id+"F0.wireOp",EDGE,"E1.right");var subQ8=sQuery(id+"F0.wireOp",EDGE,"E1.top");var subQ9=sQuery(id+"F0.wireOp",EDGE,"E1.left");var subQ10=sQuery(id+"F0.wireOp",EDGE,"E23.filletArc");var subQ11=sQuery(id+"F0.wireOp",EDGE,"E24.filletArc");Q0=makeQuery(id+"F2.boolean.opBoolean","SPLIT",FACE,{"disambiguationData":[TD([makeQuery(id+"F1.opExtrude","SWEPT_FACE",FACE,{"disambiguationData":[OSD([subQ6])]})])],"derivedFrom":makeQuery(id+"F1.opExtrude","CAP_FACE",FACE,{"disambiguationData":[OSD([subQ6,subQ8,subQ9,subQ7,subQ4,subQ3,subQ2,subQ1,subQ0,subQ5,subQ10,subQ11])],"isStart":true})});}
            var sketch = newSketch(context, id + "F16", { "sketchPlane" : qUnion([Q0])});
            skLineSegment(sketch, "E79", {"start": v(0, 74.25) * mm, "end": v(0, 104.25) * mm, "construction": true});
            skCircle(sketch, "E80", {"center": v(0, 104.25) * mm, "radius": 6 * mm});
            skLineSegment(sketch, "E81", {"start": v(-33, 74.25) * mm, "end": v(-15, 92.25) * mm});
            skLineSegment(sketch, "E82", {"start": v(33, 74.25) * mm, "end": v(15, 92.25) * mm});
            skLineSegment(sketch, "E83", {"start": v(-15, 92.25) * mm, "end": v(-15, 104.25) * mm});
            skLineSegment(sketch, "E84", {"start": v(15, 92.25) * mm, "end": v(15, 104.25) * mm});
            skArc(sketch, "E85", {"start": v(15, 104.25) * mm, "mid": v(0, 119.25) * mm, "end": v(-15, 104.25) * mm});
            skLineSegment(sketch, "E86", {"start": v(-74.25, 0) * mm, "end": v(74.25, 0) * mm, "construction": true});
            skLineSegment(sketch, "E87.MirrorCS", {"start": v(-33, -74.25) * mm, "end": v(-15, -92.25) * mm});
            skLineSegment(sketch, "E88.MirrorCS", {"start": v(-15, -92.25) * mm, "end": v(-15, -104.25) * mm});
            skArc(sketch, "E89.MirrorCS", {"start": v(15, -104.25) * mm, "mid": v(0, -119.25) * mm, "end": v(-15, -104.25) * mm});
            skCircle(sketch, "E90.MirrorC", {"center": v(0, -104.25) * mm, "radius": 6 * mm});
            skLineSegment(sketch, "E91.MirrorCS", {"start": v(0, -74.25) * mm, "end": v(0, -104.25) * mm, "construction": true});
            skLineSegment(sketch, "E92.MirrorCS", {"start": v(15, -92.25) * mm, "end": v(15, -104.25) * mm});
            skLineSegment(sketch, "E93.MirrorCS", {"start": v(33, -74.25) * mm, "end": v(15, -92.25) * mm});
            skSolve(sketch);
        }
        {
            var Q0;
            Q0=makeQuery(id+"F16.imprint","IMPRINT",FACE,{"disambiguationData":[TD([[makeQuery(id+"F16.imprint","IMPRINT",EDGE,{"derivedFrom":makeQuery(id+"F1.opExtrude","CAP_EDGE",EDGE,{"disambiguationData":[OSD([sQuery(id+"F0.wireOp",EDGE,"E1.left")])],"isStart":true})}),-1.0]])]});
            var Q1;
            {var subQ0=sQuery(id+"F16.wireOp",EDGE,"E87.MirrorCS");Q1=makeQuery(id+"F16.imprint","IMPRINT",FACE,{"disambiguationData":[TD([[makeQuery(id+"F16.imprint","IMPRINT",EDGE,{"derivedFrom":subQ0}),1.0]])]});}
            var Q2;
            Q2=makeQuery(id+"F16.imprint","IMPRINT",FACE,{"disambiguationData":[TD([[makeQuery(id+"F16.imprint","IMPRINT",EDGE,{"derivedFrom":sQuery(id+"F16.wireOp",EDGE,"E80")}),-1.0]])]});
            var Q3;
            Q3=makeQuery(id+"F2.opExtrude","CAP_FACE",FACE,{"disambiguationData":[OSD([sQuery(id+"F0.wireOp",EDGE,"E12"),sQuery(id+"F0.wireOp",EDGE,"E13"),sQuery(id+"F0.wireOp",EDGE,"E14"),sQuery(id+"F0.wireOp",EDGE,"E15"),sQuery(id+"F0.wireOp",EDGE,"E17.filletArc"),sQuery(id+"F0.wireOp",EDGE,"E18.filletArc"),sQuery(id+"F0.wireOp",EDGE,"E19.filletArc"),sQuery(id+"F0.wireOp",EDGE,"E20.filletArc"),sQuery(id+"F0.wireOp",EDGE,"E25.0"),sQuery(id+"F0.wireOp",EDGE,"E25.1"),sQuery(id+"F0.wireOp",EDGE,"E25.2"),sQuery(id+"F0.wireOp",EDGE,"E25.3"),sQuery(id+"F0.wireOp",EDGE,"E25.4"),sQuery(id+"F0.wireOp",EDGE,"E25.5"),sQuery(id+"F0.wireOp",EDGE,"E25.6"),sQuery(id+"F0.wireOp",EDGE,"E25.7")])],"isStart":false});
            extrude(context, id + "F17", {"entities" : qUnion([Q0, Q1, Q2]), "endBound" : BoundingType.UP_TO_SURFACE, "endBoundEntityFace" : qUnion([Q3]), "depth" : 25 * mm});
        }
    });
